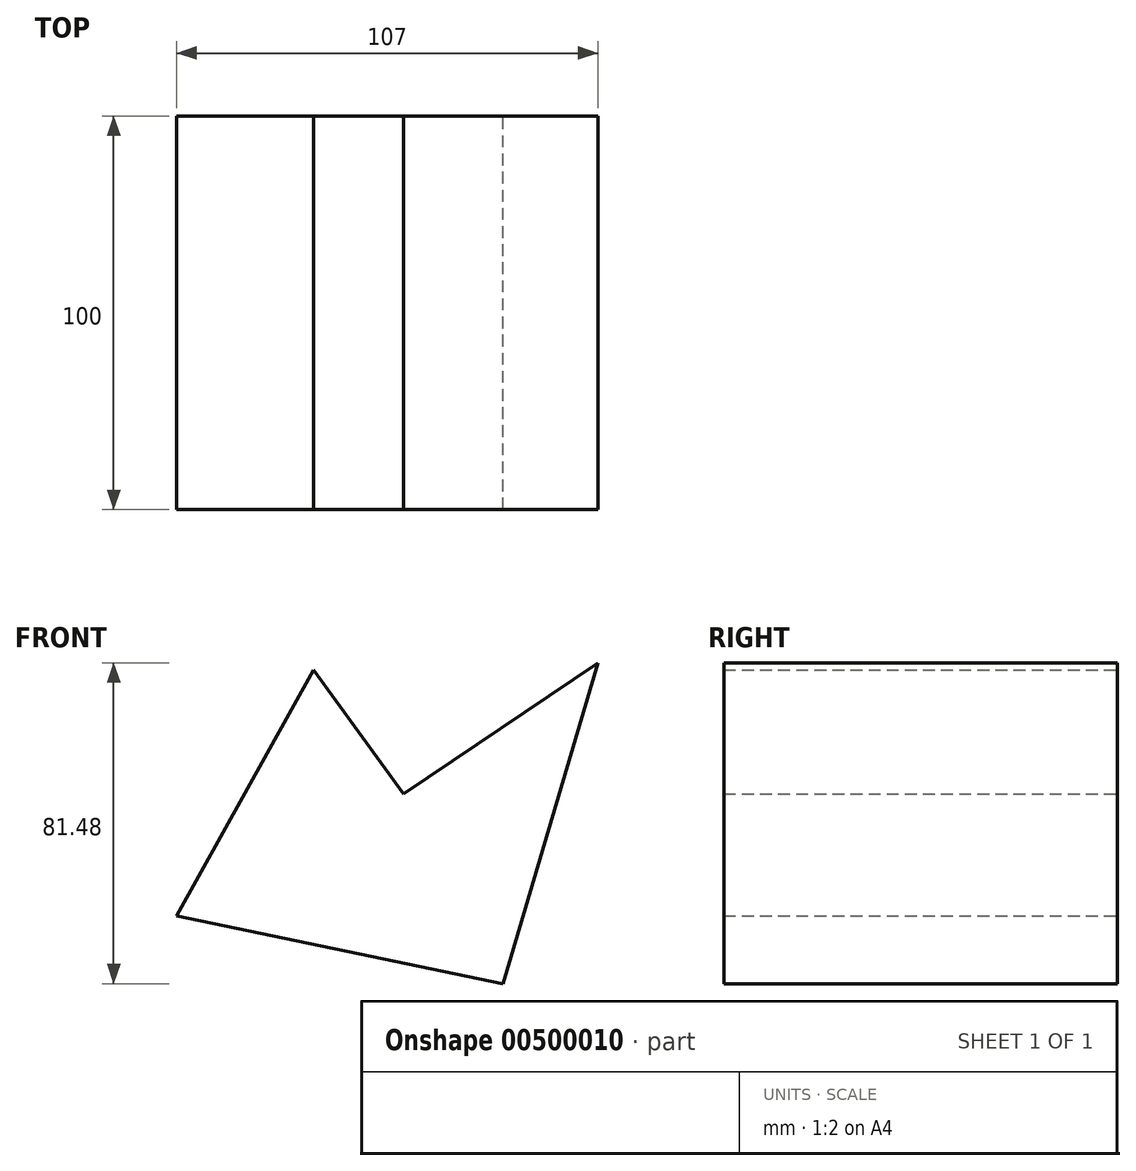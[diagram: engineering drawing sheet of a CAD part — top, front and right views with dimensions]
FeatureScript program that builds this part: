
annotation { "Feature Type Name" : "Feature", "Feature Type Description" : "" }
export const myFeature = defineFeature(function(context is Context, id is Id, definition is map)
    precondition{}
    {
        {
            var Q0;
            Q0=qCreatedBy(makeId("Front.planeOp"),FACE);
            var sketch = newSketch(context, id + "F0", { "sketchPlane" : qUnion([Q0])});
            skLineSegment(sketch, "E0", {"start": v(-22.66, 45.18) * mm, "end": v(-57.66, -17.64) * mm});
            skLineSegment(sketch, "E1", {"start": v(-22.95, 44.9) * mm, "end": v(0, 13.34) * mm});
            skLineSegment(sketch, "E2", {"start": v(0, 13.34) * mm, "end": v(49.34, 46.62) * mm});
            skLineSegment(sketch, "E3", {"start": v(49.34, 46.62) * mm, "end": v(25.25, -34.86) * mm});
            skLineSegment(sketch, "E4", {"start": v(25.25, -34.86) * mm, "end": v(-57.66, -17.64) * mm});
            skSolve(sketch);
        }
        {
            var Q0;
            {var subQ0=sQuery(id+"F0.wireOp",EDGE,"E2");Q0=makeQuery(id+"F0.imprint","IMPRINT",FACE,{"disambiguationData":[TD([[makeQuery(id+"F0.imprint","IMPRINT",EDGE,{"derivedFrom":subQ0}),-1.0]])]});}
            extrude(context, id + "F1", {"entities" : qUnion([Q0]), "endBound" : BoundingType.SYMMETRIC, "depth" : 100 * mm});
        }
    });
